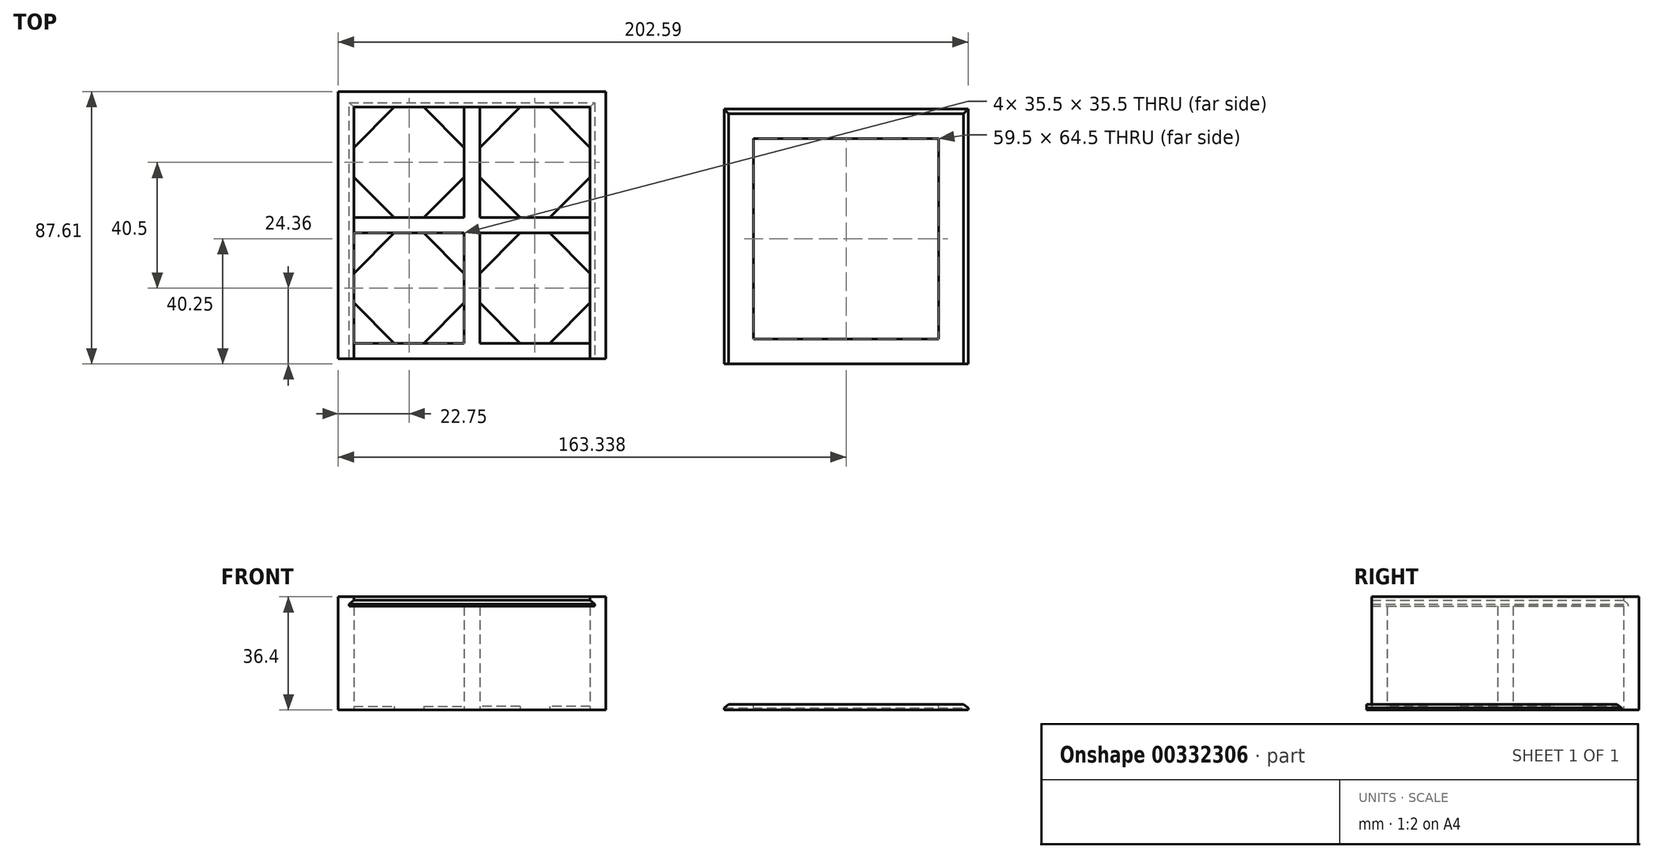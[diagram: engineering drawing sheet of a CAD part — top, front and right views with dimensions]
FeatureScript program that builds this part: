
annotation { "Feature Type Name" : "Feature", "Feature Type Description" : "" }
export const myFeature = defineFeature(function(context is Context, id is Id, definition is map)
    precondition{}
    {
        {
            var Q0;
            Q0=qCreatedBy(makeId("Top.planeOp"),FACE);
            var sketch = newSketch(context, id + "F0", { "sketchPlane" : qUnion([Q0])});
            skLineSegment(sketch, "E0.bottom", {"start": v(-2.5, 38) * mm, "end": v(-38, 38) * mm});
            skLineSegment(sketch, "E0.top", {"start": v(-2.5, 2.5) * mm, "end": v(-38, 2.5) * mm});
            skLineSegment(sketch, "E0.left", {"start": v(-2.5, 38) * mm, "end": v(-2.5, 2.5) * mm});
            skLineSegment(sketch, "E0.right", {"start": v(-38, 38) * mm, "end": v(-38, 2.5) * mm});
            skPoint(sketch, "E0.middle", {"position": v(-20.25, 20.25) * mm});
            skLineSegment(sketch, "E1.MirrorCS", {"start": v(-2.5, -38) * mm, "end": v(-38, -38) * mm});
            skPoint(sketch, "E2.MirrorP", {"position": v(-20.25, -20.25) * mm});
            skLineSegment(sketch, "E3.MirrorCS", {"start": v(-38, -38) * mm, "end": v(-38, -2.5) * mm});
            skLineSegment(sketch, "E4.MirrorCS", {"start": v(-2.5, -38) * mm, "end": v(-2.5, -2.5) * mm});
            skLineSegment(sketch, "E5.MirrorCS", {"start": v(-2.5, -2.5) * mm, "end": v(-38, -2.5) * mm});
            skLineSegment(sketch, "E6.MirrorCS", {"start": v(2.5, -2.5) * mm, "end": v(38, -2.5) * mm});
            skLineSegment(sketch, "E7.MirrorCS", {"start": v(2.5, -38) * mm, "end": v(2.5, -2.5) * mm});
            skPoint(sketch, "E8.MirrorP", {"position": v(20.25, 20.25) * mm});
            skLineSegment(sketch, "E9.MirrorCS", {"start": v(2.5, 38) * mm, "end": v(38, 38) * mm});
            skLineSegment(sketch, "E10.MirrorCS", {"start": v(2.5, 2.5) * mm, "end": v(38, 2.5) * mm});
            skLineSegment(sketch, "E11.MirrorCS", {"start": v(2.5, 38) * mm, "end": v(2.5, 2.5) * mm});
            skLineSegment(sketch, "E12.MirrorCS", {"start": v(38, 38) * mm, "end": v(38, 2.5) * mm});
            skLineSegment(sketch, "E13.MirrorCS", {"start": v(2.5, -38) * mm, "end": v(38, -38) * mm});
            skLineSegment(sketch, "E14.MirrorCS", {"start": v(38, -38) * mm, "end": v(38, -2.5) * mm});
            skPoint(sketch, "E15.MirrorP", {"position": v(20.25, -20.25) * mm});
            skLineSegment(sketch, "E16.bottom", {"start": v(43, 43) * mm, "end": v(-43, 43) * mm});
            skLineSegment(sketch, "E16.top", {"start": v(43, -43) * mm, "end": v(-43, -43) * mm});
            skLineSegment(sketch, "E16.left", {"start": v(43, 43) * mm, "end": v(43, -43) * mm});
            skLineSegment(sketch, "E16.right", {"start": v(-43, 43) * mm, "end": v(-43, -43) * mm});
            skPoint(sketch, "E16.middle", {"position": v(0, 0) * mm});
            skLineSegment(sketch, "E17", {"start": v(-25, 38) * mm, "end": v(-38, 25) * mm});
            skLineSegment(sketch, "E18", {"start": v(-38, 20.25) * mm, "end": v(-2.5, 20.25) * mm, "construction": true});
            skLineSegment(sketch, "E19", {"start": v(-20.25, 38) * mm, "end": v(-20.25, 2.5) * mm, "construction": true});
            skLineSegment(sketch, "E20.MirrorCS", {"start": v(-15.5, 38) * mm, "end": v(-2.5, 25) * mm});
            skLineSegment(sketch, "E21.MirrorCS", {"start": v(-25, 2.5) * mm, "end": v(-38, 15.5) * mm});
            skLineSegment(sketch, "E22.MirrorCS", {"start": v(-15.5, 2.5) * mm, "end": v(-2.5, 15.5) * mm});
            skLineSegment(sketch, "E23", {"start": v(-38, 38) * mm, "end": v(-31.5, 31.5) * mm, "construction": true});
            skLineSegment(sketch, "E24.MirrorCS", {"start": v(-25, -2.5) * mm, "end": v(-38, -15.5) * mm});
            skLineSegment(sketch, "E25.MirrorCS", {"start": v(-15.5, -2.5) * mm, "end": v(-2.5, -15.5) * mm});
            skLineSegment(sketch, "E26.MirrorCS", {"start": v(-15.5, -38) * mm, "end": v(-2.5, -25) * mm});
            skLineSegment(sketch, "E27.MirrorCS", {"start": v(-25, -38) * mm, "end": v(-38, -25) * mm});
            skLineSegment(sketch, "E28.MirrorCS", {"start": v(15.5, 38) * mm, "end": v(2.5, 25) * mm});
            skLineSegment(sketch, "E29.MirrorCS", {"start": v(25, 38) * mm, "end": v(38, 25) * mm});
            skLineSegment(sketch, "E30.MirrorCS", {"start": v(25, 2.5) * mm, "end": v(38, 15.5) * mm});
            skLineSegment(sketch, "E31.MirrorCS", {"start": v(15.5, 2.5) * mm, "end": v(2.5, 15.5) * mm});
            skLineSegment(sketch, "E32.MirrorCS", {"start": v(25, -2.5) * mm, "end": v(38, -15.5) * mm});
            skLineSegment(sketch, "E33.MirrorCS", {"start": v(25, -38) * mm, "end": v(38, -25) * mm});
            skLineSegment(sketch, "E34.MirrorCS", {"start": v(15.5, -38) * mm, "end": v(2.5, -25) * mm});
            skLineSegment(sketch, "E35.MirrorCS", {"start": v(15.5, -2.5) * mm, "end": v(2.5, -15.5) * mm});
            skLineSegment(sketch, "E36.bottom", {"start": v(81.09, 37.39) * mm, "end": v(159.59, 37.39) * mm});
            skLineSegment(sketch, "E36.top", {"start": v(81.09, -44.61) * mm, "end": v(159.59, -44.61) * mm});
            skLineSegment(sketch, "E36.left", {"start": v(81.09, 37.39) * mm, "end": v(81.09, -44.61) * mm});
            skLineSegment(sketch, "E36.right", {"start": v(159.59, 37.39) * mm, "end": v(159.59, -44.61) * mm});
            skSolve(sketch);
        }
        {
            var Q0;
            Q0=makeQuery(id+"F0.imprint","IMPRINT",FACE,{"disambiguationData":[TD([[makeQuery(id+"F0.imprint","IMPRINT",EDGE,{"derivedFrom":sQuery(id+"F0.wireOp",EDGE,"E16.bottom")}),1.0]])]});
            var Q1;
            {var subQ3=sQuery(id+"F0.wireOp",EDGE,"E17");Q1=makeQuery(id+"F0.imprint","IMPRINT",FACE,{"disambiguationData":[TD([[makeQuery(id+"F0.imprint","IMPRINT",EDGE,{"derivedFrom":subQ3}),-1.0]])]});}
            var Q2;
            {var subQ3=sQuery(id+"F0.wireOp",EDGE,"E21.MirrorCS");Q2=makeQuery(id+"F0.imprint","IMPRINT",FACE,{"disambiguationData":[TD([[makeQuery(id+"F0.imprint","IMPRINT",EDGE,{"derivedFrom":subQ3}),1.0]])]});}
            var Q3;
            {var subQ3=sQuery(id+"F0.wireOp",EDGE,"E22.MirrorCS");Q3=makeQuery(id+"F0.imprint","IMPRINT",FACE,{"disambiguationData":[TD([[makeQuery(id+"F0.imprint","IMPRINT",EDGE,{"derivedFrom":subQ3}),-1.0]])]});}
            var Q4;
            {var subQ3=sQuery(id+"F0.wireOp",EDGE,"E20.MirrorCS");Q4=makeQuery(id+"F0.imprint","IMPRINT",FACE,{"disambiguationData":[TD([[makeQuery(id+"F0.imprint","IMPRINT",EDGE,{"derivedFrom":subQ3}),1.0]])]});}
            var Q5;
            {var subQ3=sQuery(id+"F0.wireOp",EDGE,"E28.MirrorCS");Q5=makeQuery(id+"F0.imprint","IMPRINT",FACE,{"disambiguationData":[TD([[makeQuery(id+"F0.imprint","IMPRINT",EDGE,{"derivedFrom":subQ3}),-1.0]])]});}
            var Q6;
            {var subQ3=sQuery(id+"F0.wireOp",EDGE,"E29.MirrorCS");Q6=makeQuery(id+"F0.imprint","IMPRINT",FACE,{"disambiguationData":[TD([[makeQuery(id+"F0.imprint","IMPRINT",EDGE,{"derivedFrom":subQ3}),1.0]])]});}
            var Q7;
            {var subQ3=sQuery(id+"F0.wireOp",EDGE,"E30.MirrorCS");Q7=makeQuery(id+"F0.imprint","IMPRINT",FACE,{"disambiguationData":[TD([[makeQuery(id+"F0.imprint","IMPRINT",EDGE,{"derivedFrom":subQ3}),-1.0]])]});}
            var Q8;
            {var subQ3=sQuery(id+"F0.wireOp",EDGE,"E31.MirrorCS");Q8=makeQuery(id+"F0.imprint","IMPRINT",FACE,{"disambiguationData":[TD([[makeQuery(id+"F0.imprint","IMPRINT",EDGE,{"derivedFrom":subQ3}),1.0]])]});}
            var Q9;
            {var subQ3=sQuery(id+"F0.wireOp",EDGE,"E24.MirrorCS");Q9=makeQuery(id+"F0.imprint","IMPRINT",FACE,{"disambiguationData":[TD([[makeQuery(id+"F0.imprint","IMPRINT",EDGE,{"derivedFrom":subQ3}),-1.0]])]});}
            var Q10;
            {var subQ3=sQuery(id+"F0.wireOp",EDGE,"E25.MirrorCS");Q10=makeQuery(id+"F0.imprint","IMPRINT",FACE,{"disambiguationData":[TD([[makeQuery(id+"F0.imprint","IMPRINT",EDGE,{"derivedFrom":subQ3}),1.0]])]});}
            var Q11;
            {var subQ3=sQuery(id+"F0.wireOp",EDGE,"E27.MirrorCS");Q11=makeQuery(id+"F0.imprint","IMPRINT",FACE,{"disambiguationData":[TD([[makeQuery(id+"F0.imprint","IMPRINT",EDGE,{"derivedFrom":subQ3}),1.0]])]});}
            var Q12;
            {var subQ3=sQuery(id+"F0.wireOp",EDGE,"E26.MirrorCS");Q12=makeQuery(id+"F0.imprint","IMPRINT",FACE,{"disambiguationData":[TD([[makeQuery(id+"F0.imprint","IMPRINT",EDGE,{"derivedFrom":subQ3}),-1.0]])]});}
            var Q13;
            {var subQ3=sQuery(id+"F0.wireOp",EDGE,"E34.MirrorCS");Q13=makeQuery(id+"F0.imprint","IMPRINT",FACE,{"disambiguationData":[TD([[makeQuery(id+"F0.imprint","IMPRINT",EDGE,{"derivedFrom":subQ3}),1.0]])]});}
            var Q14;
            {var subQ3=sQuery(id+"F0.wireOp",EDGE,"E35.MirrorCS");Q14=makeQuery(id+"F0.imprint","IMPRINT",FACE,{"disambiguationData":[TD([[makeQuery(id+"F0.imprint","IMPRINT",EDGE,{"derivedFrom":subQ3}),-1.0]])]});}
            var Q15;
            {var subQ3=sQuery(id+"F0.wireOp",EDGE,"E32.MirrorCS");Q15=makeQuery(id+"F0.imprint","IMPRINT",FACE,{"disambiguationData":[TD([[makeQuery(id+"F0.imprint","IMPRINT",EDGE,{"derivedFrom":subQ3}),1.0]])]});}
            var Q16;
            {var subQ3=sQuery(id+"F0.wireOp",EDGE,"E33.MirrorCS");Q16=makeQuery(id+"F0.imprint","IMPRINT",FACE,{"disambiguationData":[TD([[makeQuery(id+"F0.imprint","IMPRINT",EDGE,{"derivedFrom":subQ3}),-1.0]])]});}
            extrude(context, id + "F1", {"entities" : qUnion([Q0, Q1, Q2, Q3, Q4, Q5, Q6, Q7, Q8, Q9, Q10, Q11, Q12, Q13, Q14, Q15, Q16]), "depth" : 1.2 * mm});
        }
        {
            var Q0;
            Q0=makeQuery(id+"F0.imprint","IMPRINT",FACE,{"disambiguationData":[TD([[makeQuery(id+"F0.imprint","IMPRINT",EDGE,{"derivedFrom":sQuery(id+"F0.wireOp",EDGE,"E16.bottom")}),1.0]])]});
            extrude(context, id + "F2", {"entities" : qUnion([Q0]), "operationType" : NewBodyOperationType.ADD, "depth" : 33.4 * mm});
        }
        {
            var Q0;
            Q0=makeQuery(id+"F2.opExtrude","CAP_FACE",FACE,{"disambiguationData":[OSD([sQuery(id+"F0.wireOp",EDGE,"E0.bottom"),sQuery(id+"F0.wireOp",EDGE,"E0.top"),sQuery(id+"F0.wireOp",EDGE,"E0.left"),sQuery(id+"F0.wireOp",EDGE,"E0.right"),sQuery(id+"F0.wireOp",EDGE,"E1.MirrorCS"),sQuery(id+"F0.wireOp",EDGE,"E3.MirrorCS"),sQuery(id+"F0.wireOp",EDGE,"E4.MirrorCS"),sQuery(id+"F0.wireOp",EDGE,"E5.MirrorCS"),sQuery(id+"F0.wireOp",EDGE,"E6.MirrorCS"),sQuery(id+"F0.wireOp",EDGE,"E7.MirrorCS"),sQuery(id+"F0.wireOp",EDGE,"E9.MirrorCS"),sQuery(id+"F0.wireOp",EDGE,"E10.MirrorCS"),sQuery(id+"F0.wireOp",EDGE,"E11.MirrorCS"),sQuery(id+"F0.wireOp",EDGE,"E12.MirrorCS"),sQuery(id+"F0.wireOp",EDGE,"E13.MirrorCS"),sQuery(id+"F0.wireOp",EDGE,"E14.MirrorCS"),sQuery(id+"F0.wireOp",EDGE,"E16.bottom"),sQuery(id+"F0.wireOp",EDGE,"E16.top"),sQuery(id+"F0.wireOp",EDGE,"E16.left"),sQuery(id+"F0.wireOp",EDGE,"E16.right")])],"isStart":false});
            var sketch = newSketch(context, id + "F3", { "sketchPlane" : qUnion([Q0])});
            skLineSegment(sketch, "E37", {"start": v(-43, -43) * mm, "end": v(-43, 43) * mm});
            skLineSegment(sketch, "E38", {"start": v(-43, 43) * mm, "end": v(43, 43) * mm});
            skLineSegment(sketch, "E39", {"start": v(43, 43) * mm, "end": v(43, -43) * mm});
            skLineSegment(sketch, "E40", {"start": v(43, -43) * mm, "end": v(38, -43) * mm});
            skLineSegment(sketch, "E41", {"start": v(38, -43) * mm, "end": v(38, 38) * mm});
            skLineSegment(sketch, "E42", {"start": v(38, 38) * mm, "end": v(-38, 38) * mm});
            skLineSegment(sketch, "E43", {"start": v(-38, 38) * mm, "end": v(-38, -43) * mm});
            skLineSegment(sketch, "E44", {"start": v(-38, -43) * mm, "end": v(-43, -43) * mm});
            skSolve(sketch);
        }
        {
            var Q0;
            Q0=makeQuery(id+"F3.imprint","IMPRINT",FACE,{"disambiguationData":[TD([[makeQuery(id+"F3.imprint","IMPRINT",EDGE,{"derivedFrom":sQuery(id+"F3.wireOp",EDGE,"E37")}),1.0]])]});
            extrude(context, id + "F4", {"entities" : qUnion([Q0]), "operationType" : NewBodyOperationType.ADD, "depth" : 3 * mm});
        }
        {
            var Q0;
            {var subQ0=sQuery(id+"F0.wireOp",EDGE,"E16.top");Q0=makeQuery(id+"F4.boolean.opBoolean","MERGE",FACE,{"derivedFrom":[makeQuery(id+"F2.boolean.opBoolean","MERGE",FACE,{"derivedFrom":[makeQuery(id+"F1.opExtrude","SWEPT_FACE",FACE,{"disambiguationData":[OSD([subQ0])]}),makeQuery(id+"F2.opExtrude","SWEPT_FACE",FACE,{"disambiguationData":[OSD([subQ0])]})]}),makeQuery(id+"F4.opExtrude","SWEPT_FACE",FACE,{"disambiguationData":[OSD([sQuery(id+"F3.wireOp",EDGE,"E40")])]}),makeQuery(id+"F4.opExtrude","SWEPT_FACE",FACE,{"disambiguationData":[OSD([sQuery(id+"F3.wireOp",EDGE,"E44")])]})]});}
            var sketch = newSketch(context, id + "F5", { "sketchPlane" : qUnion([Q0])});
            skLineSegment(sketch, "E45.bottom", {"start": v(-43, 36.4) * mm, "end": v(-38, 36.4) * mm, "construction": true});
            skLineSegment(sketch, "E45.top", {"start": v(-43, 33.4) * mm, "end": v(-38, 33.4) * mm, "construction": true});
            skLineSegment(sketch, "E45.left", {"start": v(-43, 36.4) * mm, "end": v(-43, 33.4) * mm, "construction": true});
            skLineSegment(sketch, "E45.right", {"start": v(-38, 36.4) * mm, "end": v(-38, 33.4) * mm, "construction": true});
            skLineSegment(sketch, "E46", {"start": v(-39.5, 33.4) * mm, "end": v(-38, 33.4) * mm});
            skLineSegment(sketch, "E47", {"start": v(-38, 35.3) * mm, "end": v(-38, 33.4) * mm});
            skLineSegment(sketch, "E48", {"start": v(-38, 33.4) * mm, "end": v(-39.5, 33.4) * mm});
            skLineSegment(sketch, "E49", {"start": v(-39.5, 33.4) * mm, "end": v(-39.5, 34) * mm});
            skLineSegment(sketch, "E50", {"start": v(-39.5, 34) * mm, "end": v(-38, 35.3) * mm});
            skSolve(sketch);
        }
        {
            var Q0;
            {var subQ0=sQuery(id+"F0.wireOp",EDGE,"E3.MirrorCS");var subQ1=sQuery(id+"F0.wireOp",EDGE,"E0.right");Q0=makeQuery(id+"F4.boolean.opBoolean","MERGE",FACE,{"derivedFrom":[makeQuery(id+"F2.boolean.opBoolean","MERGE",FACE,{"derivedFrom":[makeQuery(id+"F1.opExtrude","SWEPT_FACE",FACE,{"disambiguationData":[OSD([subQ1])]}),makeQuery(id+"F2.opExtrude","SWEPT_FACE",FACE,{"disambiguationData":[OSD([subQ1])]})]}),makeQuery(id+"F2.boolean.opBoolean","MERGE",FACE,{"derivedFrom":[makeQuery(id+"F1.opExtrude","SWEPT_FACE",FACE,{"disambiguationData":[OSD([subQ0])]}),makeQuery(id+"F2.opExtrude","SWEPT_FACE",FACE,{"disambiguationData":[OSD([subQ0])]})]}),makeQuery(id+"F4.opExtrude","SWEPT_FACE",FACE,{"disambiguationData":[OSD([sQuery(id+"F3.wireOp",EDGE,"E43")])]})]});}
            var sketch = newSketch(context, id + "F6", { "sketchPlane" : qUnion([Q0])});
            skLineSegment(sketch, "E51", {"start": v(-43, 35.3) * mm, "end": v(38, 35.3) * mm});
            skSolve(sketch);
        }
        {
            var Q0;
            {var subQ0=sQuery(id+"F0.wireOp",EDGE,"E9.MirrorCS");var subQ1=sQuery(id+"F0.wireOp",EDGE,"E0.bottom");Q0=makeQuery(id+"F4.boolean.opBoolean","MERGE",FACE,{"derivedFrom":[makeQuery(id+"F2.boolean.opBoolean","MERGE",FACE,{"derivedFrom":[makeQuery(id+"F1.opExtrude","SWEPT_FACE",FACE,{"disambiguationData":[OSD([subQ1])]}),makeQuery(id+"F2.opExtrude","SWEPT_FACE",FACE,{"disambiguationData":[OSD([subQ1])]})]}),makeQuery(id+"F2.boolean.opBoolean","MERGE",FACE,{"derivedFrom":[makeQuery(id+"F1.opExtrude","SWEPT_FACE",FACE,{"disambiguationData":[OSD([subQ0])]}),makeQuery(id+"F2.opExtrude","SWEPT_FACE",FACE,{"disambiguationData":[OSD([subQ0])]})]}),makeQuery(id+"F4.opExtrude","SWEPT_FACE",FACE,{"disambiguationData":[OSD([sQuery(id+"F3.wireOp",EDGE,"E42")])]})]});}
            var sketch = newSketch(context, id + "F7", { "sketchPlane" : qUnion([Q0])});
            skLineSegment(sketch, "E52", {"start": v(-38, 35.3) * mm, "end": v(38, 35.3) * mm});
            skSolve(sketch);
        }
        {
            var Q0;
            {var subQ0=sQuery(id+"F0.wireOp",EDGE,"E14.MirrorCS");var subQ1=sQuery(id+"F0.wireOp",EDGE,"E12.MirrorCS");Q0=makeQuery(id+"F4.boolean.opBoolean","MERGE",FACE,{"derivedFrom":[makeQuery(id+"F2.boolean.opBoolean","MERGE",FACE,{"derivedFrom":[makeQuery(id+"F1.opExtrude","SWEPT_FACE",FACE,{"disambiguationData":[OSD([subQ1])]}),makeQuery(id+"F2.opExtrude","SWEPT_FACE",FACE,{"disambiguationData":[OSD([subQ1])]})]}),makeQuery(id+"F2.boolean.opBoolean","MERGE",FACE,{"derivedFrom":[makeQuery(id+"F1.opExtrude","SWEPT_FACE",FACE,{"disambiguationData":[OSD([subQ0])]}),makeQuery(id+"F2.opExtrude","SWEPT_FACE",FACE,{"disambiguationData":[OSD([subQ0])]})]}),makeQuery(id+"F4.opExtrude","SWEPT_FACE",FACE,{"disambiguationData":[OSD([sQuery(id+"F3.wireOp",EDGE,"E41")])]})]});}
            var sketch = newSketch(context, id + "F8", { "sketchPlane" : qUnion([Q0])});
            skLineSegment(sketch, "E53", {"start": v(-38, 35.3) * mm, "end": v(43, 35.3) * mm});
            skSolve(sketch);
        }
        {
            var Q0;
            Q0=makeQuery(id+"F0.imprint","IMPRINT",FACE,{"disambiguationData":[TD([[makeQuery(id+"F0.imprint","IMPRINT",EDGE,{"derivedFrom":sQuery(id+"F0.wireOp",EDGE,"E36.bottom")}),-1.0]])]});
            extrude(context, id + "F9", {"entities" : qUnion([Q0]), "depth" : 1.8 * mm});
        }
        {
            var Q0;
            Q0=makeQuery(id+"F9.opExtrude","SWEPT_FACE",FACE,{"disambiguationData":[OSD([sQuery(id+"F0.wireOp",EDGE,"E36.top")])]});
            var sketch = newSketch(context, id + "F10", { "sketchPlane" : qUnion([Q0])});
            skLineSegment(sketch, "E54", {"start": v(81.09, 0) * mm, "end": v(81.09, 0.6) * mm});
            skLineSegment(sketch, "E55", {"start": v(81.09, 0.6) * mm, "end": v(82.59, 1.8) * mm});
            skLineSegment(sketch, "E56", {"start": v(82.59, 1.8) * mm, "end": v(82.59, 0) * mm});
            skLineSegment(sketch, "E57", {"start": v(82.59, 0) * mm, "end": v(81.09, 0) * mm});
            skSolve(sketch);
        }
        {
            var Q0;
            Q0=makeQuery(id+"F5.imprint","IMPRINT",FACE,{"disambiguationData":[TD([[makeQuery(id+"F5.imprint","IMPRINT",EDGE,{"derivedFrom":sQuery(id+"F5.wireOp",EDGE,"E47")}),-1.0]])]});
            var Q1;
            Q1=sQuery(id+"F6.wireOp",EDGE,"E51");
            var Q2;
            Q2=sQuery(id+"F7.wireOp",EDGE,"E52");
            var Q3;
            Q3=sQuery(id+"F8.wireOp",EDGE,"E53");
            sweep(context, id + "F11", {"operationType" : NewBodyOperationType.REMOVE, "profiles" : qUnion([Q0]), "path" : qUnion([Q1, Q2, Q3])});
        }
        {
            var Q0;
            {var subQ0=sQuery(id+"F10.wireOp",EDGE,"E55");Q0=makeQuery(id+"F10.imprint","IMPRINT",FACE,{"disambiguationData":[TD([[makeQuery(id+"F10.imprint","IMPRINT",EDGE,{"derivedFrom":subQ0}),1.0]])]});}
            var Q1;
            Q1=sQuery(id+"F0.wireOp",EDGE,"E36.left");
            var Q2;
            Q2=sQuery(id+"F0.wireOp",EDGE,"E36.bottom");
            var Q3;
            Q3=sQuery(id+"F0.wireOp",EDGE,"E36.right");
            sweep(context, id + "F12", {"operationType" : NewBodyOperationType.REMOVE, "profiles" : qUnion([Q0]), "path" : qUnion([Q1, Q2, Q3])});
        }
        {
            var Q0;
            Q0=makeQuery(id+"F9.opExtrude","CAP_FACE",FACE,{"disambiguationData":[OSD([sQuery(id+"F0.wireOp",EDGE,"E36.bottom"),sQuery(id+"F0.wireOp",EDGE,"E36.top"),sQuery(id+"F0.wireOp",EDGE,"E36.left"),sQuery(id+"F0.wireOp",EDGE,"E36.right")])],"isStart":false});
            var sketch = newSketch(context, id + "F13", { "sketchPlane" : qUnion([Q0])});
            skLineSegment(sketch, "E58.bottom", {"start": v(150.09, -36.61) * mm, "end": v(90.59, -36.61) * mm});
            skLineSegment(sketch, "E58.top", {"start": v(150.09, 27.89) * mm, "end": v(90.59, 27.89) * mm});
            skLineSegment(sketch, "E58.left", {"start": v(150.09, -36.61) * mm, "end": v(150.09, 27.89) * mm});
            skLineSegment(sketch, "E58.right", {"start": v(90.59, -36.61) * mm, "end": v(90.59, 27.89) * mm});
            skPoint(sketch, "E58.middle", {"position": v(120.34, -4.36) * mm});
            skPoint(sketch, "E58.middle.positionSnap0", {"position": v(158.09, -4.36) * mm});
            skPoint(sketch, "E58.middle.positionSnap1", {"position": v(120.34, 35.89) * mm});
            skPoint(sketch, "E58.centerSnap0", {"position": v(158.09, -4.36) * mm});
            skPoint(sketch, "E58.centerSnap1", {"position": v(120.34, 35.89) * mm});
            skSolve(sketch);
        }
        {
            var Q0;
            Q0=makeQuery(id+"F13.imprint","IMPRINT",FACE,{"disambiguationData":[TD([[makeQuery(id+"F13.imprint","IMPRINT",EDGE,{"derivedFrom":sQuery(id+"F13.wireOp",EDGE,"E58.bottom")}),-1.0]])]});
            extrude(context, id + "F14", {"entities" : qUnion([Q0]), "operationType" : NewBodyOperationType.REMOVE, "endBound" : BoundingType.THROUGH_ALL, "oppositeDirection" : true, "depth" : 25 * mm});
        }
    });
